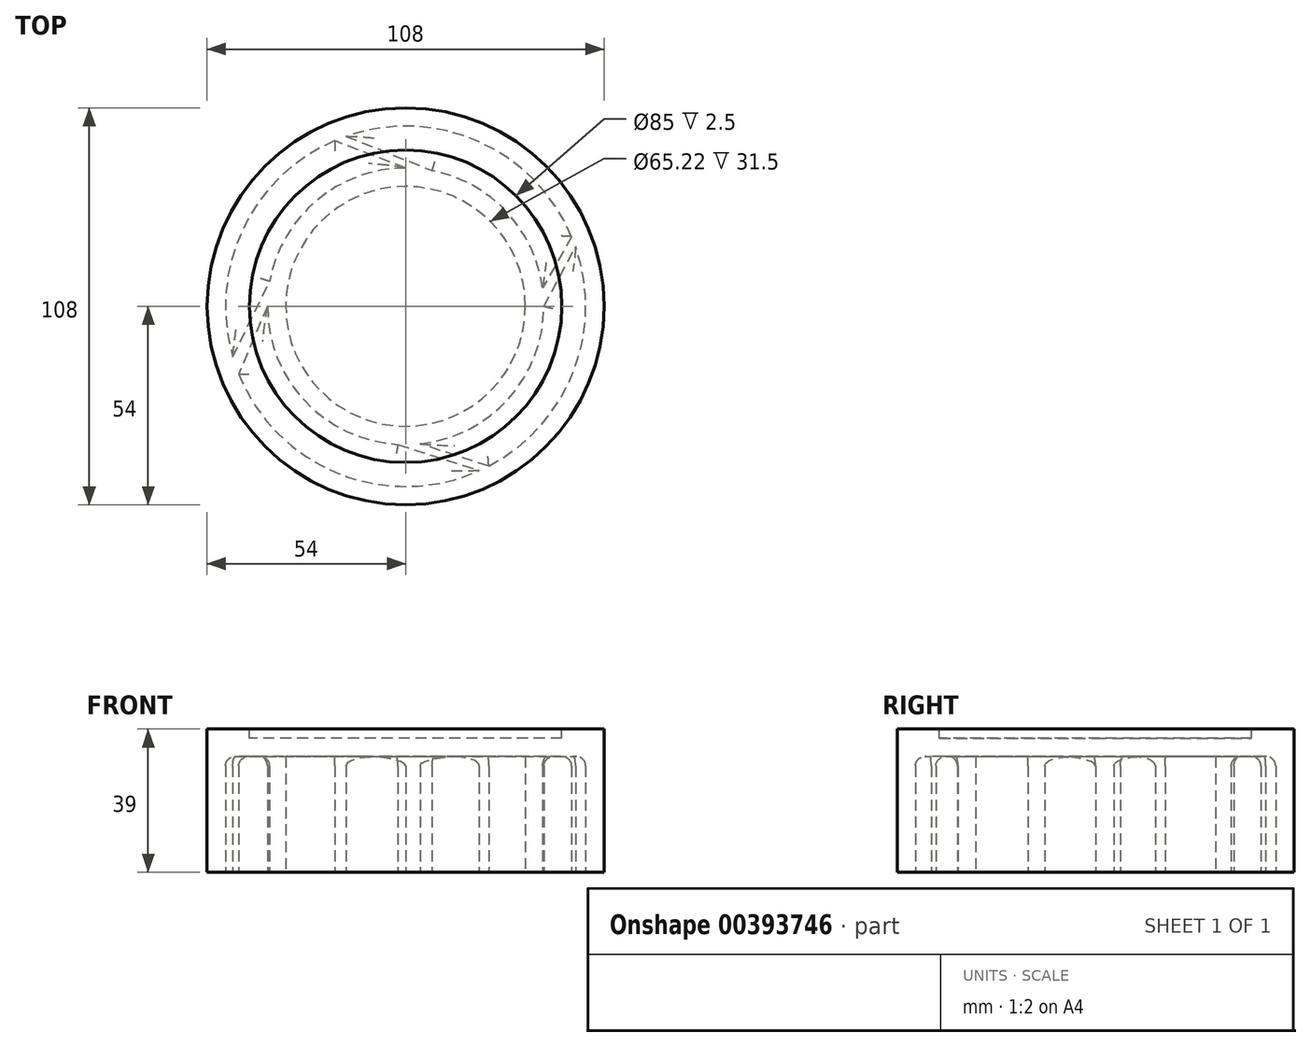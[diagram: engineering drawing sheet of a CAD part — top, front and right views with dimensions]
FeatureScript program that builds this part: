
annotation { "Feature Type Name" : "Feature", "Feature Type Description" : "" }
export const myFeature = defineFeature(function(context is Context, id is Id, definition is map)
    precondition{}
    {
        {
            var Q0;
            Q0=qCreatedBy(makeId("Top.planeOp"),FACE);
            var sketch = newSketch(context, id + "F0", { "sketchPlane" : qUnion([Q0])});
            skCircle(sketch, "E0", {"center": v(0, 0) * mm, "radius": 54 * mm});
            skLineSegment(sketch, "E1", {"start": v(0, 0) * mm, "end": v(-0.15, 54) * mm});
            skSolve(sketch);
        }
        {
            var Q0;
            Q0=makeQuery(id+"F0.imprint","IMPRINT",FACE,{"disambiguationData":[TD([[makeQuery(id+"F0.imprint","IMPRINT",EDGE,{"derivedFrom":sQuery(id+"F0.wireOp",EDGE,"E0")}),1.0]])]});
            extrude(context, id + "F1", {"entities" : qUnion([Q0]), "depth" : 39 * mm});
        }
        {
            var Q0;
            Q0=makeQuery(id+"F1.opExtrude","CAP_FACE",FACE,{"disambiguationData":[OSD([sQuery(id+"F0.wireOp",EDGE,"E0")])],"isStart":false});
            var sketch = newSketch(context, id + "F2", { "sketchPlane" : qUnion([Q0])});
            skCircle(sketch, "E2", {"center": v(0, 0) * mm, "radius": 42.5 * mm});
            skLineSegment(sketch, "E3", {"start": v(0, 0) * mm, "end": v(1.23, 42.48) * mm, "construction": true});
            skSolve(sketch);
        }
        {
            var Q0;
            Q0=makeQuery(id+"F2.imprint","IMPRINT",FACE,{"disambiguationData":[TD([[makeQuery(id+"F2.imprint","IMPRINT",EDGE,{"derivedFrom":sQuery(id+"F2.wireOp",EDGE,"E2")}),1.0]])]});
            extrude(context, id + "F3", {"entities" : qUnion([Q0]), "operationType" : NewBodyOperationType.REMOVE, "oppositeDirection" : true, "depth" : 2.5 * mm});
        }
        {
            var Q0;
            Q0=makeQuery(id+"F0.imprint","IMPRINT",FACE,{"disambiguationData":[TD([[makeQuery(id+"F0.imprint","IMPRINT",EDGE,{"derivedFrom":sQuery(id+"F0.wireOp",EDGE,"E0")}),1.0]])]});
            var sketch = newSketch(context, id + "F4", { "sketchPlane" : qUnion([Q0])});
            skCircle(sketch, "E4.0", {"center": v(0, 0) * mm, "radius": 49 * mm});
            skCircle(sketch, "E5", {"center": v(0, 0) * mm, "radius": 32.61 * mm});
            skCircle(sketch, "E6.0", {"center": v(0, 0) * mm, "radius": 37.61 * mm});
            skLineSegment(sketch, "E7", {"start": v(0, 37.61) * mm, "end": v(-19.31, 45.03) * mm});
            skLineSegment(sketch, "E8", {"start": v(-16.17, 46.26) * mm, "end": v(7.22, 36.91) * mm});
            skLineSegment(sketch, "E9", {"start": v(-2.08, -37.55) * mm, "end": v(20.05, -44.7) * mm});
            skLineSegment(sketch, "E10", {"start": v(22.64, -43.46) * mm, "end": v(3.92, -37.4) * mm});
            skLineSegment(sketch, "E11", {"start": v(37.61, 0) * mm, "end": v(46.24, 16.23) * mm});
            skLineSegment(sketch, "E12", {"start": v(45.18, 18.96) * mm, "end": v(37.28, 5) * mm});
            skLineSegment(sketch, "E13", {"start": v(-37.61, 0) * mm, "end": v(-45.4, -18.43) * mm});
            skLineSegment(sketch, "E14", {"start": v(-47.02, -13.8) * mm, "end": v(-37, 6.76) * mm});
            skSolve(sketch);
        }
        {
            var Q0;
            {var subQ0=sQuery(id+"F4.wireOp",EDGE,"E7");Q0=makeQuery(id+"F4.imprint","IMPRINT",FACE,{"disambiguationData":[TD([[makeQuery(id+"F4.imprint","IMPRINT",EDGE,{"derivedFrom":subQ0}),1.0]])]});}
            var Q1;
            {var subQ0=sQuery(id+"F4.wireOp",EDGE,"E9");Q1=makeQuery(id+"F4.imprint","IMPRINT",FACE,{"disambiguationData":[TD([[makeQuery(id+"F4.imprint","IMPRINT",EDGE,{"derivedFrom":subQ0}),-1.0]])]});}
            var Q2;
            {var subQ0=sQuery(id+"F4.wireOp",EDGE,"E10");Q2=makeQuery(id+"F4.imprint","IMPRINT",FACE,{"disambiguationData":[TD([[makeQuery(id+"F4.imprint","IMPRINT",EDGE,{"derivedFrom":subQ0}),-1.0]])]});}
            var Q3;
            {var subQ0=sQuery(id+"F4.wireOp",EDGE,"E8");Q3=makeQuery(id+"F4.imprint","IMPRINT",FACE,{"disambiguationData":[TD([[makeQuery(id+"F4.imprint","IMPRINT",EDGE,{"derivedFrom":subQ0}),1.0]])]});}
            var Q4;
            Q4=makeQuery(id+"F4.imprint","IMPRINT",FACE,{"disambiguationData":[TD([[makeQuery(id+"F4.imprint","IMPRINT",EDGE,{"derivedFrom":sQuery(id+"F4.wireOp",EDGE,"E5")}),1.0]])]});
            extrude(context, id + "F5", {"entities" : qUnion([Q0, Q1, Q2, Q3, Q4]), "operationType" : NewBodyOperationType.REMOVE, "depth" : 31.5 * mm});
        }
        {
            var Q0;
            Q0=makeQuery(id+"F5.boolean.opBoolean","COPY",FACE,{"derivedFrom":makeQuery(id+"F5.opExtrude","CAP_FACE",FACE,{"disambiguationData":[OSD([sQuery(id+"F4.wireOp",EDGE,"E4.0"),sQuery(id+"F4.wireOp",EDGE,"E6.0"),sQuery(id+"F4.wireOp",EDGE,"E9"),sQuery(id+"F4.wireOp",EDGE,"E13")])],"isStart":false})});
            var Q1;
            Q1=makeQuery(id+"F5.boolean.opBoolean","COPY",FACE,{"derivedFrom":makeQuery(id+"F5.opExtrude","CAP_FACE",FACE,{"disambiguationData":[OSD([sQuery(id+"F4.wireOp",EDGE,"E4.0"),sQuery(id+"F4.wireOp",EDGE,"E6.0"),sQuery(id+"F4.wireOp",EDGE,"E10"),sQuery(id+"F4.wireOp",EDGE,"E11")])],"isStart":false})});
            var Q2;
            Q2=makeQuery(id+"F5.boolean.opBoolean","COPY",FACE,{"derivedFrom":makeQuery(id+"F5.opExtrude","CAP_FACE",FACE,{"disambiguationData":[OSD([sQuery(id+"F4.wireOp",EDGE,"E4.0"),sQuery(id+"F4.wireOp",EDGE,"E6.0"),sQuery(id+"F4.wireOp",EDGE,"E8"),sQuery(id+"F4.wireOp",EDGE,"E12")])],"isStart":false})});
            var Q3;
            Q3=makeQuery(id+"F5.boolean.opBoolean","COPY",FACE,{"derivedFrom":makeQuery(id+"F5.opExtrude","CAP_FACE",FACE,{"disambiguationData":[OSD([sQuery(id+"F4.wireOp",EDGE,"E4.0"),sQuery(id+"F4.wireOp",EDGE,"E6.0"),sQuery(id+"F4.wireOp",EDGE,"E7"),sQuery(id+"F4.wireOp",EDGE,"E14")])],"isStart":false})});
            fillet(context, id + "F6", {"entities" : qUnion([Q0, Q1, Q2, Q3]), "radius" : 2.5 * mm, "tangentPropagation" : true, "allowEdgeOverflow" : false});
        }
    });
